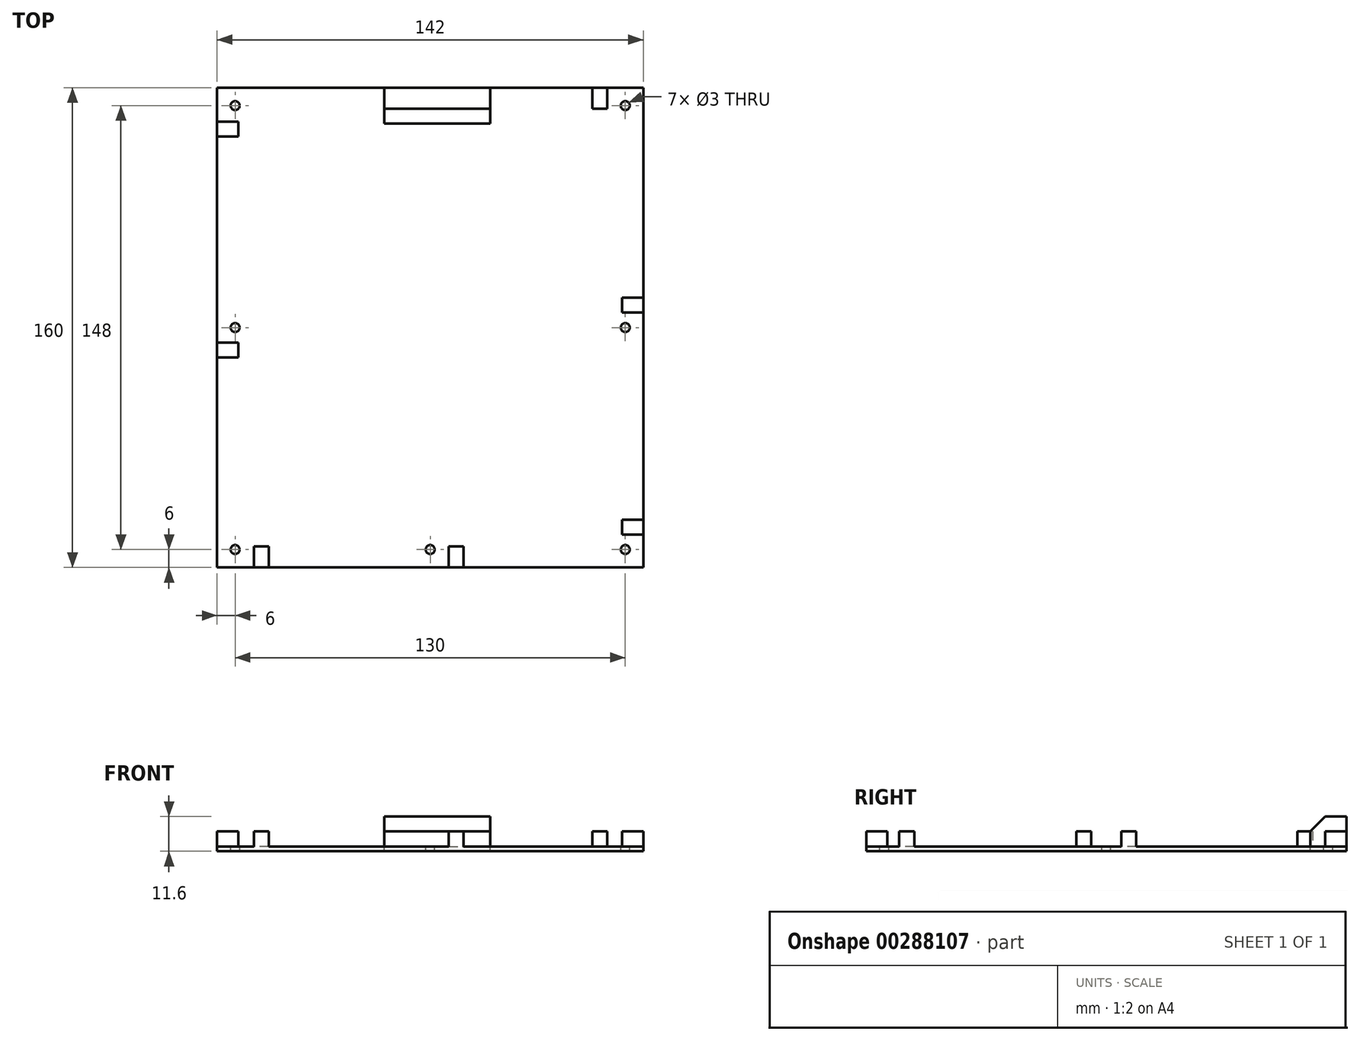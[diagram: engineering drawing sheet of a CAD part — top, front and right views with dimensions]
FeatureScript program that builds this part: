
annotation { "Feature Type Name" : "Feature", "Feature Type Description" : "" }
export const myFeature = defineFeature(function(context is Context, id is Id, definition is map)
    precondition{}
    {
        {
            var Q0;
            Q0=qCreatedBy(makeId("Top.planeOp"),FACE);
            var sketch = newSketch(context, id + "F0", { "sketchPlane" : qUnion([Q0])});
            skLineSegment(sketch, "E0.bottom", {"start": v(0, 0) * mm, "end": v(142, 0) * mm});
            skLineSegment(sketch, "E0.left", {"start": v(0, 0) * mm, "end": v(0, 160) * mm});
            skLineSegment(sketch, "E0.right", {"start": v(142, 0) * mm, "end": v(142, 160) * mm});
            skLineSegment(sketch, "E1", {"start": v(0, 160) * mm, "end": v(55.7, 160) * mm});
            skLineSegment(sketch, "E2", {"start": v(55.7, 160) * mm, "end": v(55.7, 148) * mm});
            skLineSegment(sketch, "E3", {"start": v(55.7, 148) * mm, "end": v(91, 148) * mm});
            skLineSegment(sketch, "E4", {"start": v(91, 148) * mm, "end": v(91, 160) * mm});
            skLineSegment(sketch, "E5", {"start": v(91, 160) * mm, "end": v(142, 160) * mm});
            skCircle(sketch, "E6", {"center": v(6, 154) * mm, "radius": 1.5 * mm});
            skCircle(sketch, "E7", {"center": v(6, 80) * mm, "radius": 1.5 * mm});
            skCircle(sketch, "E8", {"center": v(6, 6) * mm, "radius": 1.5 * mm});
            skCircle(sketch, "E9", {"center": v(71, 6) * mm, "radius": 1.5 * mm});
            skCircle(sketch, "E10", {"center": v(136, 6) * mm, "radius": 1.5 * mm});
            skCircle(sketch, "E11", {"center": v(136, 80) * mm, "radius": 1.5 * mm});
            skCircle(sketch, "E12", {"center": v(136, 154) * mm, "radius": 1.5 * mm});
            skSolve(sketch);
        }
        {
            var Q0;
            Q0 = qSketchRegion(id + "F0", true);
            extrude(context, id + "F1", {"entities" : qUnion([Q0]), "oppositeDirection" : true, "depth" : 1.6 * mm});
        }
        {
            var Q0;
            Q0=qCreatedBy(makeId("Top.planeOp"),FACE);
            var sketch = newSketch(context, id + "F2", { "sketchPlane" : qUnion([Q0])});
            skLineSegment(sketch, "E13.bottom", {"start": v(55.7, 148) * mm, "end": v(91, 148) * mm});
            skLineSegment(sketch, "E13.top", {"start": v(55.7, 160) * mm, "end": v(91, 160) * mm});
            skLineSegment(sketch, "E13.left", {"start": v(55.7, 148) * mm, "end": v(55.7, 160) * mm});
            skLineSegment(sketch, "E13.right", {"start": v(91, 148) * mm, "end": v(91, 160) * mm});
            skSolve(sketch);
        }
        {
            var Q0;
            Q0 = qSketchRegion(id + "F2", true);
            extrude(context, id + "F3", {"entities" : qUnion([Q0]), "depth" : 10 * mm});
        }
        {
            var Q0;
            Q0=qCreatedBy(makeId("Top.planeOp"),FACE);
            var sketch = newSketch(context, id + "F4", { "sketchPlane" : qUnion([Q0])});
            skLineSegment(sketch, "E14.bottom", {"start": v(0, 148.7) * mm, "end": v(7, 148.7) * mm});
            skLineSegment(sketch, "E14.top", {"start": v(0, 143.7) * mm, "end": v(7, 143.7) * mm});
            skLineSegment(sketch, "E14.left", {"start": v(0, 148.7) * mm, "end": v(0, 143.7) * mm});
            skLineSegment(sketch, "E14.right", {"start": v(7, 148.7) * mm, "end": v(7, 143.7) * mm});
            skLineSegment(sketch, "E15.bottom", {"start": v(0, 75) * mm, "end": v(7, 75) * mm});
            skLineSegment(sketch, "E15.top", {"start": v(0, 70) * mm, "end": v(7, 70) * mm});
            skLineSegment(sketch, "E15.left", {"start": v(0, 75) * mm, "end": v(0, 70) * mm});
            skLineSegment(sketch, "E15.right", {"start": v(7, 75) * mm, "end": v(7, 70) * mm});
            skLineSegment(sketch, "E16.bottom", {"start": v(125, 160) * mm, "end": v(130, 160) * mm});
            skLineSegment(sketch, "E16.top", {"start": v(125, 153) * mm, "end": v(130, 153) * mm});
            skLineSegment(sketch, "E16.left", {"start": v(125, 160) * mm, "end": v(125, 153) * mm});
            skLineSegment(sketch, "E16.right", {"start": v(130, 160) * mm, "end": v(130, 153) * mm});
            skLineSegment(sketch, "E17.bottom", {"start": v(142, 90) * mm, "end": v(135, 90) * mm});
            skLineSegment(sketch, "E17.top", {"start": v(142, 85) * mm, "end": v(135, 85) * mm});
            skLineSegment(sketch, "E17.left", {"start": v(142, 90) * mm, "end": v(142, 85) * mm});
            skLineSegment(sketch, "E17.right", {"start": v(135, 90) * mm, "end": v(135, 85) * mm});
            skLineSegment(sketch, "E18.bottom", {"start": v(142, 16) * mm, "end": v(135, 16) * mm});
            skLineSegment(sketch, "E18.top", {"start": v(142, 11) * mm, "end": v(135, 11) * mm});
            skLineSegment(sketch, "E18.left", {"start": v(142, 16) * mm, "end": v(142, 11) * mm});
            skLineSegment(sketch, "E18.right", {"start": v(135, 16) * mm, "end": v(135, 11) * mm});
            skLineSegment(sketch, "E19.bottom", {"start": v(82.17, 0) * mm, "end": v(77.17, 0) * mm});
            skLineSegment(sketch, "E19.top", {"start": v(82.17, 7) * mm, "end": v(77.17, 7) * mm});
            skLineSegment(sketch, "E19.left", {"start": v(82.17, 0) * mm, "end": v(82.17, 7) * mm});
            skLineSegment(sketch, "E19.right", {"start": v(77.17, 0) * mm, "end": v(77.17, 7) * mm});
            skLineSegment(sketch, "E20.bottom", {"start": v(17.22, 0) * mm, "end": v(12.22, 0) * mm});
            skLineSegment(sketch, "E20.top", {"start": v(17.22, 7) * mm, "end": v(12.22, 7) * mm});
            skLineSegment(sketch, "E20.left", {"start": v(17.22, 0) * mm, "end": v(17.22, 7) * mm});
            skLineSegment(sketch, "E20.right", {"start": v(12.22, 0) * mm, "end": v(12.22, 7) * mm});
            skSolve(sketch);
        }
        {
            var Q0;
            Q0 = qSketchRegion(id + "F4", true);
            extrude(context, id + "F5", {"entities" : qUnion([Q0]), "operationType" : NewBodyOperationType.ADD, "depth" : 5 * mm});
        }
        {
            var Q0;
            Q0=makeQuery(id+"F3.opExtrude","CAP_EDGE",EDGE,{"disambiguationData":[OSD([sQuery(id+"F2.wireOp",EDGE,"E13.bottom")])],"isStart":false});
            chamfer(context, id + "F6", {"entities" : qUnion([Q0]), "width" : 5 * mm, "tangentPropagation" : true});
        }
    });
